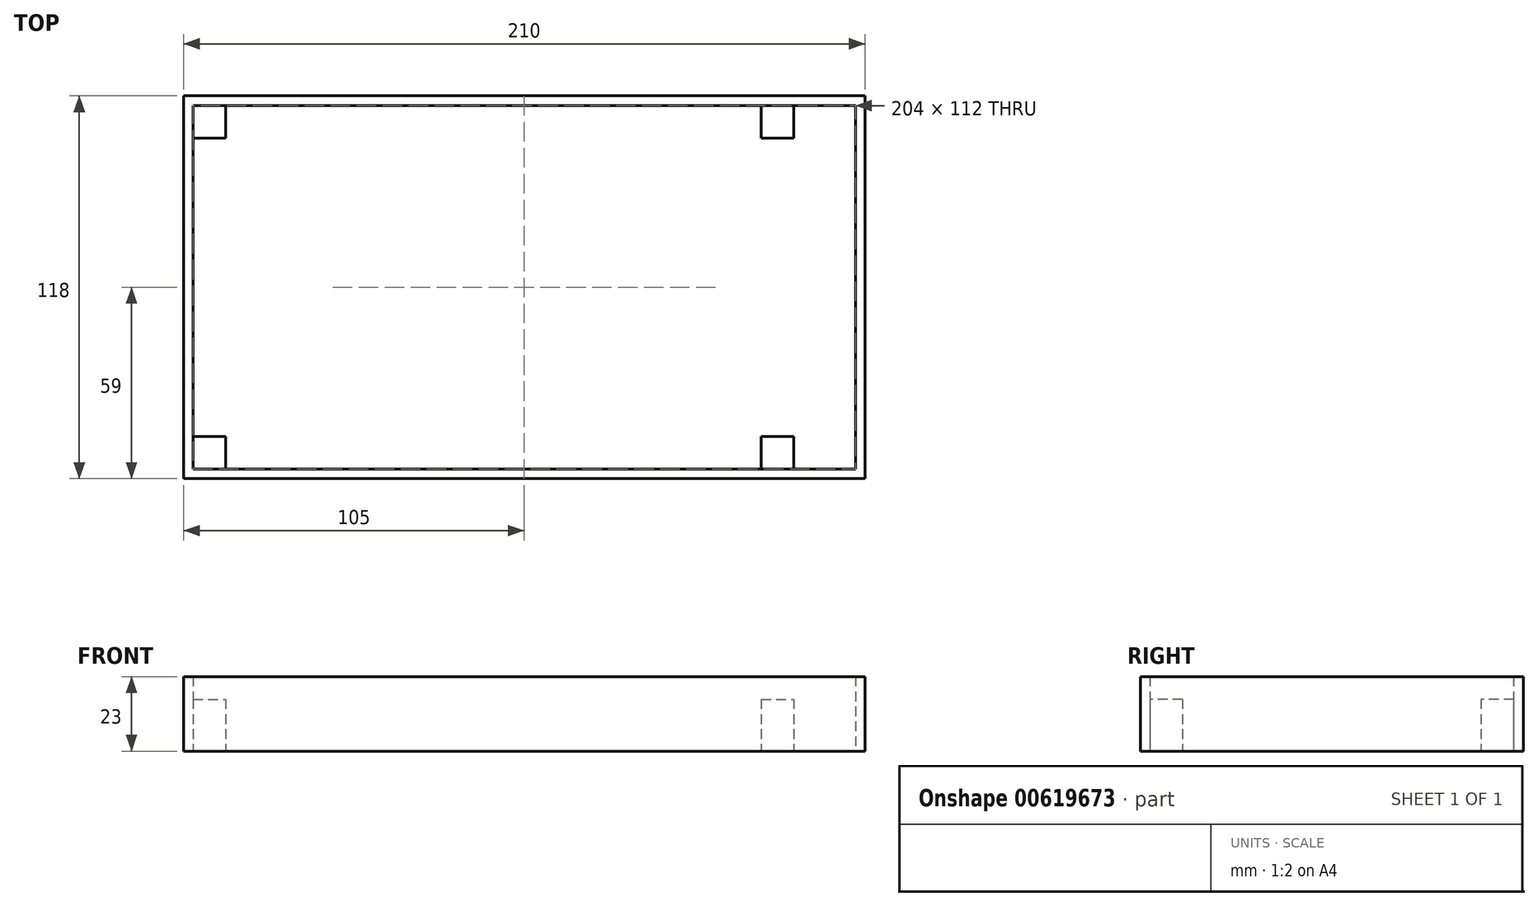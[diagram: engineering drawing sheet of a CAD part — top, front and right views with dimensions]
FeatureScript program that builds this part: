
annotation { "Feature Type Name" : "Feature", "Feature Type Description" : "" }
export const myFeature = defineFeature(function(context is Context, id is Id, definition is map)
    precondition{}
    {
        {
            var Q0;
            Q0=qCreatedBy(makeId("Top.planeOp"),FACE);
            var sketch = newSketch(context, id + "F0", { "sketchPlane" : qUnion([Q0])});
            skLineSegment(sketch, "E0.bottom", {"start": v(0, 0) * mm, "end": v(210, 0) * mm});
            skLineSegment(sketch, "E0.top", {"start": v(0, -118) * mm, "end": v(210, -118) * mm});
            skLineSegment(sketch, "E0.left", {"start": v(0, 0) * mm, "end": v(0, -118) * mm});
            skLineSegment(sketch, "E0.right", {"start": v(210, 0) * mm, "end": v(210, -118) * mm});
            skSolve(sketch);
        }
        {
            var Q0;
            Q0=makeQuery(id+"F0.imprint","IMPRINT",FACE,{"disambiguationData":[TD([[makeQuery(id+"F0.imprint","IMPRINT",EDGE,{"derivedFrom":sQuery(id+"F0.wireOp",EDGE,"E0.bottom")}),-1.0]])]});
            extrude(context, id + "F1", {"entities" : qUnion([Q0]), "depth" : 23 * mm, "offsetDistance" : 25 * mm});
        }
        {
            var Q0;
            Q0=makeQuery(id+"F1.opExtrude","CAP_FACE",FACE,{"disambiguationData":[OSD([sQuery(id+"F0.wireOp",EDGE,"E0.bottom"),sQuery(id+"F0.wireOp",EDGE,"E0.top"),sQuery(id+"F0.wireOp",EDGE,"E0.left"),sQuery(id+"F0.wireOp",EDGE,"E0.right")])],"isStart":false});
            shell(context, id + "F2", {"entities" : qUnion([Q0]), "thickness" : 3 * mm});
        }
        {
            var Q0;
            Q0=makeQuery(id+"F2.opShell","OFFSET_FACE",FACE,{"disambiguationData":[OSD([sQuery(id+"F0.wireOp",EDGE,"E0.bottom"),sQuery(id+"F0.wireOp",EDGE,"E0.top"),sQuery(id+"F0.wireOp",EDGE,"E0.left"),sQuery(id+"F0.wireOp",EDGE,"E0.right")])]});
            var sketch = newSketch(context, id + "F3", { "sketchPlane" : qUnion([Q0])});
            skLineSegment(sketch, "E1", {"start": v(3, -8) * mm, "end": v(207, -8) * mm, "construction": true});
            skLineSegment(sketch, "E2", {"start": v(3, -110) * mm, "end": v(207, -110) * mm, "construction": true});
            skLineSegment(sketch, "E3.bottom", {"start": v(3, -3) * mm, "end": v(13, -3) * mm});
            skLineSegment(sketch, "E3.top", {"start": v(3, -13) * mm, "end": v(13, -13) * mm});
            skLineSegment(sketch, "E3.left", {"start": v(3, -3) * mm, "end": v(3, -13) * mm});
            skLineSegment(sketch, "E3.right", {"start": v(13, -3) * mm, "end": v(13, -13) * mm});
            skLineSegment(sketch, "E4.bottom", {"start": v(178, -3) * mm, "end": v(188, -3) * mm});
            skLineSegment(sketch, "E4.top", {"start": v(178, -13) * mm, "end": v(188, -13) * mm});
            skLineSegment(sketch, "E4.left", {"start": v(178, -3) * mm, "end": v(178, -13) * mm});
            skLineSegment(sketch, "E4.right", {"start": v(188, -3) * mm, "end": v(188, -13) * mm});
            skLineSegment(sketch, "E5.bottom", {"start": v(3, -115) * mm, "end": v(13, -115) * mm});
            skLineSegment(sketch, "E5.top", {"start": v(3, -105) * mm, "end": v(13, -105) * mm});
            skLineSegment(sketch, "E5.left", {"start": v(3, -115) * mm, "end": v(3, -105) * mm});
            skLineSegment(sketch, "E5.right", {"start": v(13, -115) * mm, "end": v(13, -105) * mm});
            skLineSegment(sketch, "E6.bottom", {"start": v(178, -115) * mm, "end": v(188, -115) * mm});
            skLineSegment(sketch, "E6.top", {"start": v(178, -105) * mm, "end": v(188, -105) * mm});
            skLineSegment(sketch, "E6.left", {"start": v(178, -115) * mm, "end": v(178, -105) * mm});
            skLineSegment(sketch, "E6.right", {"start": v(188, -115) * mm, "end": v(188, -105) * mm});
            skSolve(sketch);
        }
        {
            var Q0;
            Q0=makeQuery(id+"F3.imprint","IMPRINT",FACE,{"disambiguationData":[TD([[makeQuery(id+"F3.imprint","IMPRINT",EDGE,{"derivedFrom":sQuery(id+"F3.wireOp",EDGE,"E3.bottom")}),-1.0]])]});
            var Q1;
            Q1=makeQuery(id+"F3.imprint","IMPRINT",FACE,{"disambiguationData":[TD([[makeQuery(id+"F3.imprint","IMPRINT",EDGE,{"derivedFrom":sQuery(id+"F3.wireOp",EDGE,"E4.bottom")}),-1.0]])]});
            var Q2;
            Q2=makeQuery(id+"F3.imprint","IMPRINT",FACE,{"disambiguationData":[TD([[makeQuery(id+"F3.imprint","IMPRINT",EDGE,{"derivedFrom":sQuery(id+"F3.wireOp",EDGE,"E6.bottom")}),1.0]])]});
            var Q3;
            Q3=makeQuery(id+"F3.imprint","IMPRINT",FACE,{"disambiguationData":[TD([[makeQuery(id+"F3.imprint","IMPRINT",EDGE,{"derivedFrom":sQuery(id+"F3.wireOp",EDGE,"E5.bottom")}),1.0]])]});
            extrude(context, id + "F4", {"entities" : qUnion([Q0, Q1, Q2, Q3]), "operationType" : NewBodyOperationType.ADD, "depth" : 13 * mm, "offsetDistance" : 25 * mm});
        }
        {
            var Q0;
            Q0=makeQuery(id+"F2.opShell","OFFSET_FACE",FACE,{"disambiguationData":[OSD([sQuery(id+"F0.wireOp",EDGE,"E0.bottom"),sQuery(id+"F0.wireOp",EDGE,"E0.top"),sQuery(id+"F0.wireOp",EDGE,"E0.left"),sQuery(id+"F0.wireOp",EDGE,"E0.right")])]});
            var sketch = newSketch(context, id + "F5", { "sketchPlane" : qUnion([Q0])});
            skLineSegment(sketch, "E7", {"start": v(3, -8) * mm, "end": v(207, -8) * mm, "construction": true});
            skLineSegment(sketch, "E8", {"start": v(207, -38) * mm, "end": v(3, -38) * mm, "construction": true});
            skCircle(sketch, "E9", {"center": v(20, -8) * mm, "radius": 1.75 * mm});
            skCircle(sketch, "E10", {"center": v(80, -8) * mm, "radius": 1.75 * mm});
            skCircle(sketch, "E11", {"center": v(20, -38) * mm, "radius": 1.75 * mm});
            skCircle(sketch, "E12", {"center": v(80, -38) * mm, "radius": 1.75 * mm});
            skLineSegment(sketch, "E13", {"start": v(207, -17.5) * mm, "end": v(3, -17.5) * mm, "construction": true});
            skCircle(sketch, "E14", {"center": v(120, -17.5) * mm, "radius": 1.75 * mm});
            skSolve(sketch);
        }
        {
            var Q0;
            Q0=makeQuery(id+"F5.imprint","IMPRINT",FACE,{"disambiguationData":[TD([[makeQuery(id+"F5.imprint","IMPRINT",EDGE,{"derivedFrom":sQuery(id+"F5.wireOp",EDGE,"E9")}),1.0]])]});
            var Q1;
            Q1=makeQuery(id+"F5.imprint","IMPRINT",FACE,{"disambiguationData":[TD([[makeQuery(id+"F5.imprint","IMPRINT",EDGE,{"derivedFrom":sQuery(id+"F5.wireOp",EDGE,"E11")}),1.0]])]});
            var Q2;
            Q2=makeQuery(id+"F5.imprint","IMPRINT",FACE,{"disambiguationData":[TD([[makeQuery(id+"F5.imprint","IMPRINT",EDGE,{"derivedFrom":sQuery(id+"F5.wireOp",EDGE,"E12")}),1.0]])]});
            var Q3;
            Q3=makeQuery(id+"F5.imprint","IMPRINT",FACE,{"disambiguationData":[TD([[makeQuery(id+"F5.imprint","IMPRINT",EDGE,{"derivedFrom":sQuery(id+"F5.wireOp",EDGE,"E10")}),1.0]])]});
            var Q4;
            Q4=makeQuery(id+"F5.imprint","IMPRINT",FACE,{"disambiguationData":[TD([[makeQuery(id+"F5.imprint","IMPRINT",EDGE,{"derivedFrom":sQuery(id+"F5.wireOp",EDGE,"E14")}),1.0]])]});
            extrude(context, id + "F6", {"entities" : qUnion([Q0, Q1, Q2, Q3, Q4]), "operationType" : NewBodyOperationType.REMOVE, "oppositeDirection" : true, "depth" : 25 * mm, "offsetDistance" : 25 * mm});
        }
        {
            var Q0;
            Q0=makeQuery(id+"F2.opShell","OFFSET_FACE",FACE,{"disambiguationData":[OSD([sQuery(id+"F0.wireOp",EDGE,"E0.bottom"),sQuery(id+"F0.wireOp",EDGE,"E0.top"),sQuery(id+"F0.wireOp",EDGE,"E0.left"),sQuery(id+"F0.wireOp",EDGE,"E0.right")])]});
            extrude(context, id + "F7", {"entities" : qUnion([Q0]), "operationType" : NewBodyOperationType.REMOVE, "oppositeDirection" : true, "depth" : 25 * mm, "offsetDistance" : 25 * mm});
        }
    });
